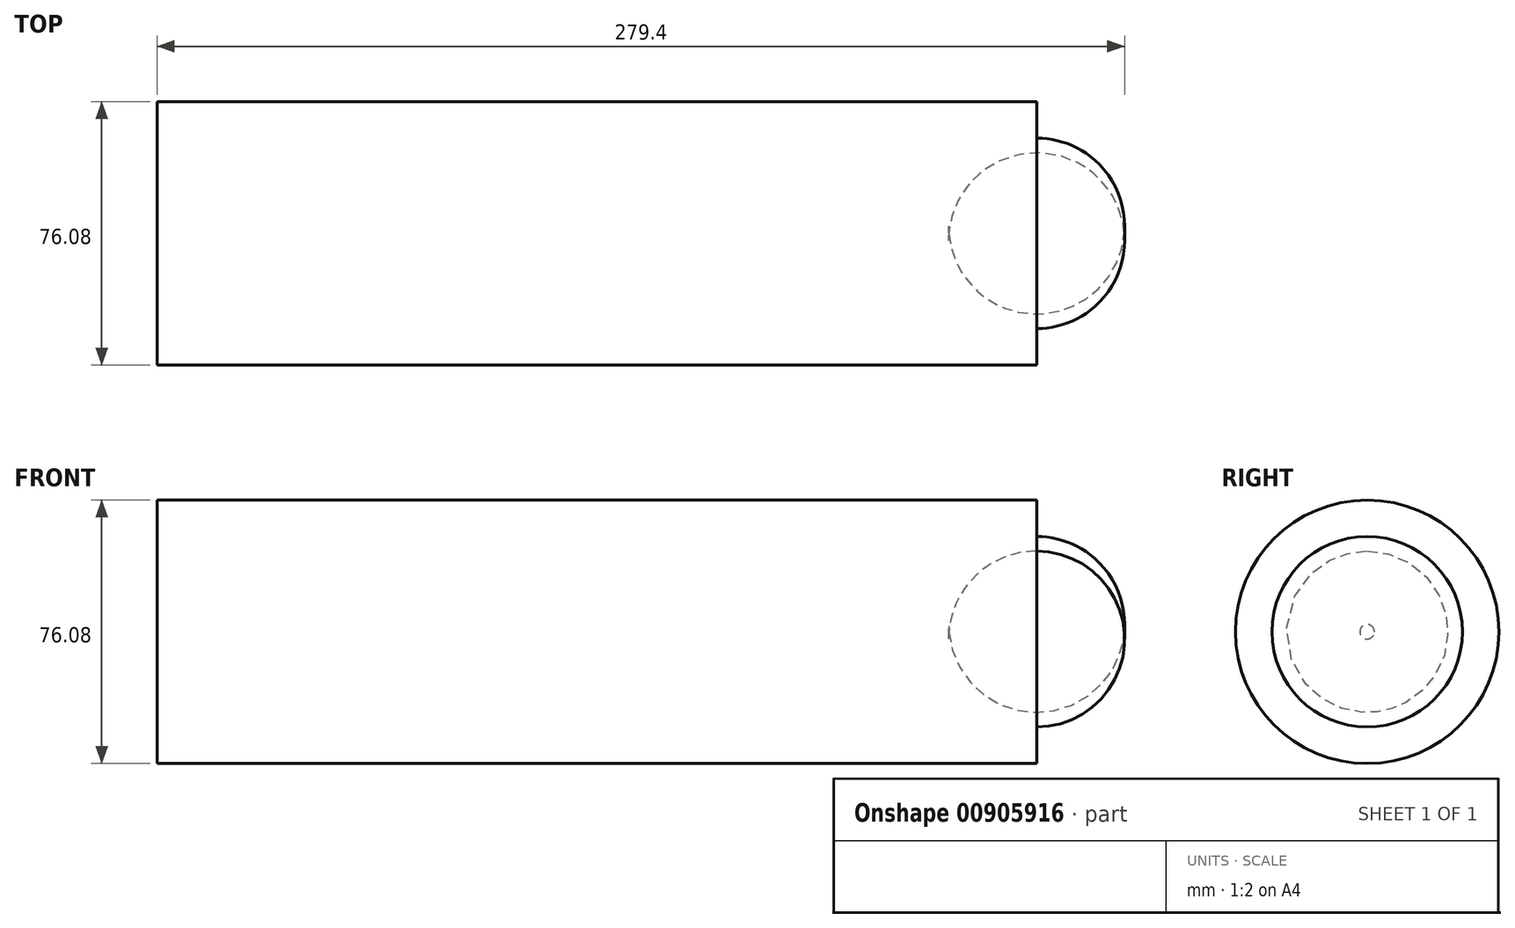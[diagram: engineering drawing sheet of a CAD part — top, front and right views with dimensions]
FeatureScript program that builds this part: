
annotation { "Feature Type Name" : "Feature", "Feature Type Description" : "" }
export const myFeature = defineFeature(function(context is Context, id is Id, definition is map)
    precondition{}
    {
        {
            var Q0;
            Q0=qCreatedBy(makeId("Right.planeOp"),FACE);
            var sketch = newSketch(context, id + "F0", { "sketchPlane" : qUnion([Q0])});
            skCircle(sketch, "E0", {"center": v(0, 0) * mm, "radius": 38.04 * mm});
            skSolve(sketch);
        }
        {
            var Q0;
            Q0 = qSketchRegion(id + "F0", true);
            var Q1;
            Q1=sQuery(id+"F0.wireOp",EDGE,"E0");
            extrude(context, id + "F1", {"entities" : qUnion([Q0]), "surfaceEntities" : qUnion([Q1]), "depth" : 254 * mm, "offsetDistance" : 25.4 * mm});
        }
        {
            var Q0;
            Q0=makeQuery(id+"F1.opExtrude","CAP_FACE",FACE,{"disambiguationData":[OSD([sQuery(id+"F0.wireOp",EDGE,"E0")])],"isStart":false});
            var sketch = newSketch(context, id + "F2", { "sketchPlane" : qUnion([Q0])});
            skCircle(sketch, "E1", {"center": v(0, 0) * mm, "radius": 27.5 * mm});
            skSolve(sketch);
        }
        {
            var Q0;
            Q0=makeQuery(id+"F2.imprint","IMPRINT",FACE,{"disambiguationData":[TD([[makeQuery(id+"F2.imprint","IMPRINT",EDGE,{"derivedFrom":sQuery(id+"F2.wireOp",EDGE,"E1")}),1.0]])]});
            var Q1;
            Q1=sQuery(id+"F2.wireOp",EDGE,"E1");
            extrude(context, id + "F3", {"entities" : qUnion([Q0]), "operationType" : NewBodyOperationType.REMOVE, "surfaceEntities" : qUnion([Q1]), "oppositeDirection" : true, "depth" : 25.4 * mm, "offsetDistance" : 25.4 * mm});
        }
        {
            var Q0;
            Q0=makeQuery(id+"F3.boolean.opBoolean","COPY",EDGE,{"derivedFrom":makeQuery(id+"F3.opExtrude","CAP_EDGE",EDGE,{"disambiguationData":[OSD([sQuery(id+"F2.wireOp",EDGE,"E1")])],"isStart":false})});
            fillet(context, id + "F4", {"entities" : qUnion([Q0]), "radius" : 25.4 * mm, "tangentPropagation" : true, "allowEdgeOverflow" : false});
        }
    });
